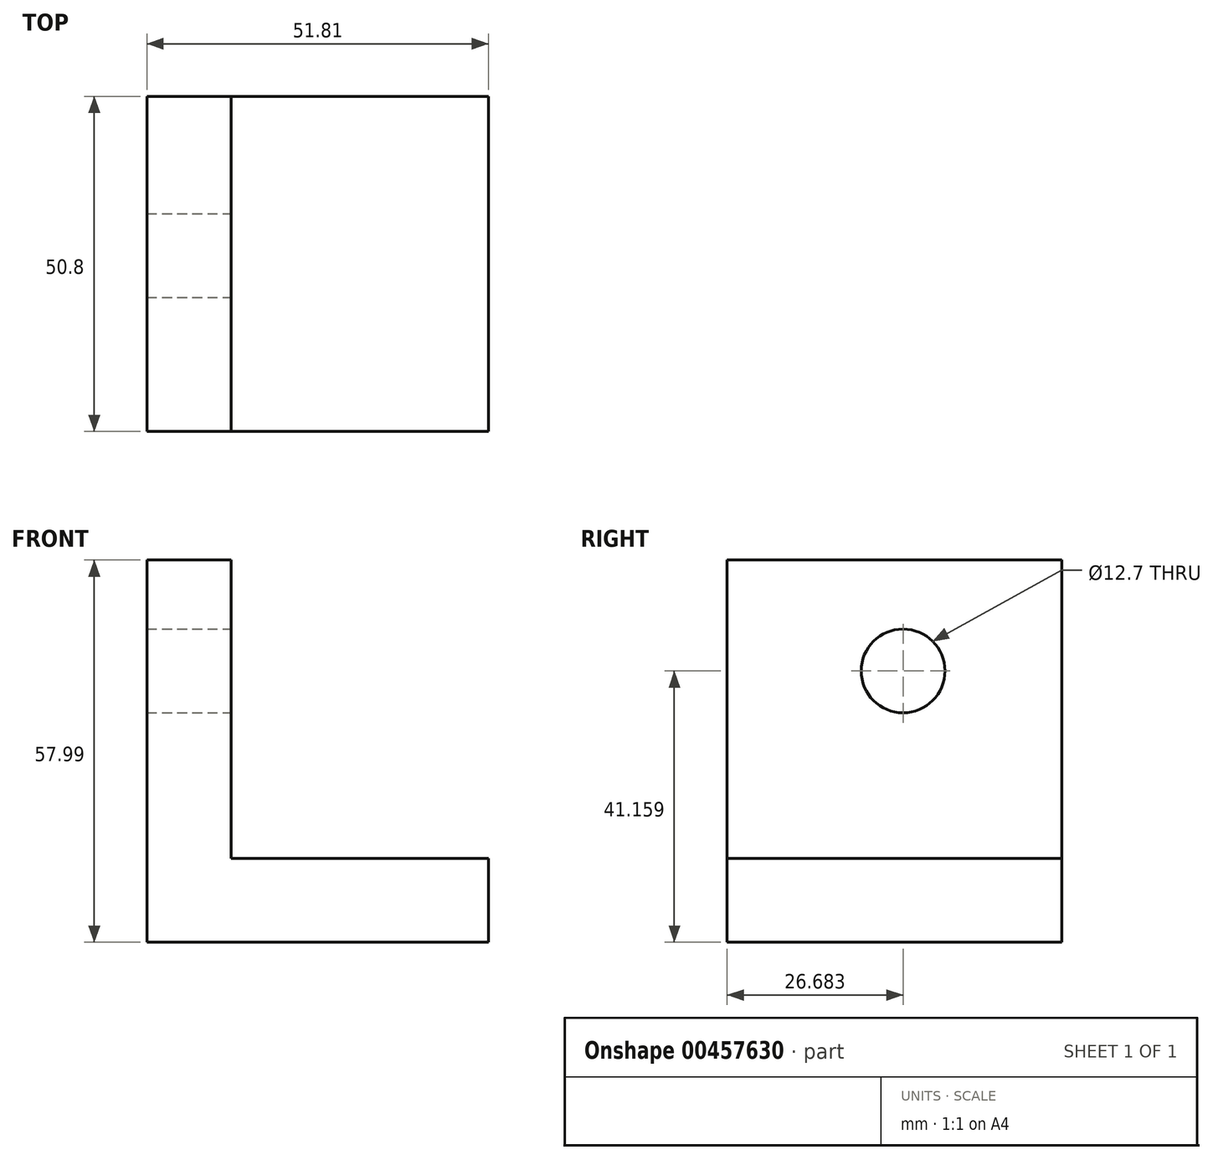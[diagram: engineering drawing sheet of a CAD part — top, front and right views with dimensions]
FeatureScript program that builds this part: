
annotation { "Feature Type Name" : "Feature", "Feature Type Description" : "" }
export const myFeature = defineFeature(function(context is Context, id is Id, definition is map)
    precondition{}
    {
        {
            var Q0;
            Q0=qCreatedBy(makeId("Front.planeOp"),FACE);
            var sketch = newSketch(context, id + "F0", { "sketchPlane" : qUnion([Q0])});
            skLineSegment(sketch, "E0.bottom", {"start": v(-49.59, 27.08) * mm, "end": v(2.22, 27.08) * mm});
            skLineSegment(sketch, "E0.top", {"start": v(-49.59, -5.51) * mm, "end": v(2.22, -5.51) * mm});
            skLineSegment(sketch, "E0.left", {"start": v(-49.59, 27.08) * mm, "end": v(-49.59, -5.51) * mm});
            skLineSegment(sketch, "E0.right", {"start": v(2.22, 27.08) * mm, "end": v(2.22, -5.51) * mm});
            skSolve(sketch);
        }
        {
            var Q0;
            Q0=makeQuery(id+"F0.imprint","IMPRINT",FACE,{"disambiguationData":[TD([[makeQuery(id+"F0.imprint","IMPRINT",EDGE,{"derivedFrom":sQuery(id+"F0.wireOp",EDGE,"E0.bottom")}),-1.0]])]});
            extrude(context, id + "F1", {"entities" : qUnion([Q0]), "depth" : 25.4 * mm});
        }
        {
            var Q0;
            Q0=makeQuery(id+"F1.opExtrude","CAP_FACE",FACE,{"disambiguationData":[OSD([sQuery(id+"F0.wireOp",EDGE,"E0.bottom"),sQuery(id+"F0.wireOp",EDGE,"E0.top"),sQuery(id+"F0.wireOp",EDGE,"E0.left"),sQuery(id+"F0.wireOp",EDGE,"E0.right")])],"isStart":false});
            extrude(context, id + "F2", {"entities" : qUnion([Q0]), "operationType" : NewBodyOperationType.ADD, "depth" : 25.4 * mm});
        }
        {
            var Q0;
            {var subQ0=sQuery(id+"F0.wireOp",EDGE,"E0.bottom");Q0=makeQuery(id+"F2.boolean.opBoolean","MERGE",FACE,{"derivedFrom":[makeQuery(id+"F1.opExtrude","SWEPT_FACE",FACE,{"disambiguationData":[OSD([subQ0])]}),makeQuery(id+"F2.opExtrude","SWEPT_FACE",FACE,{"disambiguationData":[OSD([subQ0])]})]});}
            extrude(context, id + "F3", {"entities" : qUnion([Q0]), "operationType" : NewBodyOperationType.ADD, "depth" : 25.4 * mm});
        }
        {
            var Q0;
            Q0=makeQuery(id+"F3.opExtrude","CAP_FACE",FACE,{"disambiguationData":[OSD([sQuery(id+"F0.wireOp",EDGE,"E0.bottom")])],"isStart":false});
            extrude(context, id + "F4", {"entities" : qUnion([Q0]), "operationType" : NewBodyOperationType.ADD, "depth" : -7.2 * mm});
        }
        {
            var Q0;
            Q0=makeQuery(id+"F3.opExtrude","CAP_FACE",FACE,{"disambiguationData":[OSD([sQuery(id+"F0.wireOp",EDGE,"E0.bottom")])],"isStart":false});
            var sketch = newSketch(context, id + "F5", { "sketchPlane" : qUnion([Q0])});
            skLineSegment(sketch, "E1", {"start": v(-49.59, -25.4) * mm, "end": v(-36.82, -25.4) * mm});
            skLineSegment(sketch, "E2", {"start": v(-36.82, -25.4) * mm, "end": v(-36.82, -50.8) * mm});
            skLineSegment(sketch, "E3", {"start": v(-36.82, -25.4) * mm, "end": v(-36.82, 0) * mm});
            skLineSegment(sketch, "E4", {"start": v(-36.82, -50.8) * mm, "end": v(-74.02, -87.2) * mm});
            skLineSegment(sketch, "E5", {"start": v(16.85, -19.99) * mm, "end": v(2.22, 4.46) * mm});
            skSolve(sketch);
        }
        {
            var Q0;
            {var subQ4=sQuery(id+"F5.wireOp",EDGE,"E2");Q0=makeQuery(id+"F5.imprint","IMPRINT",FACE,{"disambiguationData":[TD([[makeQuery(id+"F5.imprint","IMPRINT",EDGE,{"derivedFrom":subQ4}),1.0]])]});}
            extrude(context, id + "F6", {"entities" : qUnion([Q0]), "operationType" : NewBodyOperationType.REMOVE, "oppositeDirection" : true, "depth" : 37.85 * mm});
        }
        {
            var Q0;
            Q0=makeQuery(id+"F6.boolean.opBoolean","COPY",FACE,{"derivedFrom":makeQuery(id+"F6.opExtrude","SWEPT_FACE",FACE,{"disambiguationData":[OSD([sQuery(id+"F5.wireOp",EDGE,"E2"),sQuery(id+"F5.wireOp",EDGE,"E3")])]})});
            var sketch = newSketch(context, id + "F7", { "sketchPlane" : qUnion([Q0])});
            skCircle(sketch, "E6", {"center": v(-24.12, 35.65) * mm, "radius": 6.35 * mm});
            skSolve(sketch);
        }
        {
            var Q0;
            Q0=makeQuery(id+"F7.imprint","IMPRINT",FACE,{"disambiguationData":[TD([[makeQuery(id+"F7.imprint","IMPRINT",EDGE,{"derivedFrom":sQuery(id+"F7.wireOp",EDGE,"E6")}),1.0]])]});
            extrude(context, id + "F8", {"entities" : qUnion([Q0]), "operationType" : NewBodyOperationType.REMOVE, "oppositeDirection" : true, "depth" : 50.8 * mm});
        }
        {
            var Q0;
            Q0=makeQuery(id+"F6.boolean.opBoolean","COPY",FACE,{"derivedFrom":makeQuery(id+"F6.opExtrude","CAP_FACE",FACE,{"disambiguationData":[OSD([sQuery(id+"F0.wireOp",EDGE,"E0.bottom"),sQuery(id+"F0.wireOp",EDGE,"E0.right"),sQuery(id+"F5.wireOp",EDGE,"E2"),sQuery(id+"F5.wireOp",EDGE,"E3")])],"isStart":false})});
            extrude(context, id + "F9", {"entities" : qUnion([Q0]), "operationType" : NewBodyOperationType.REMOVE, "oppositeDirection" : true, "depth" : 4.57 * mm});
        }
        {
            var Q0;
            Q0=makeQuery(id+"F9.boolean.opBoolean","COPY",FACE,{"derivedFrom":makeQuery(id+"F9.opExtrude","CAP_FACE",FACE,{"disambiguationData":[OSD([sQuery(id+"F0.wireOp",EDGE,"E0.bottom"),sQuery(id+"F0.wireOp",EDGE,"E0.right"),sQuery(id+"F5.wireOp",EDGE,"E2"),sQuery(id+"F5.wireOp",EDGE,"E3")])],"isStart":false})});
            extrude(context, id + "F10", {"entities" : qUnion([Q0]), "operationType" : NewBodyOperationType.REMOVE, "oppositeDirection" : true, "depth" : 2.87 * mm});
        }
    });
